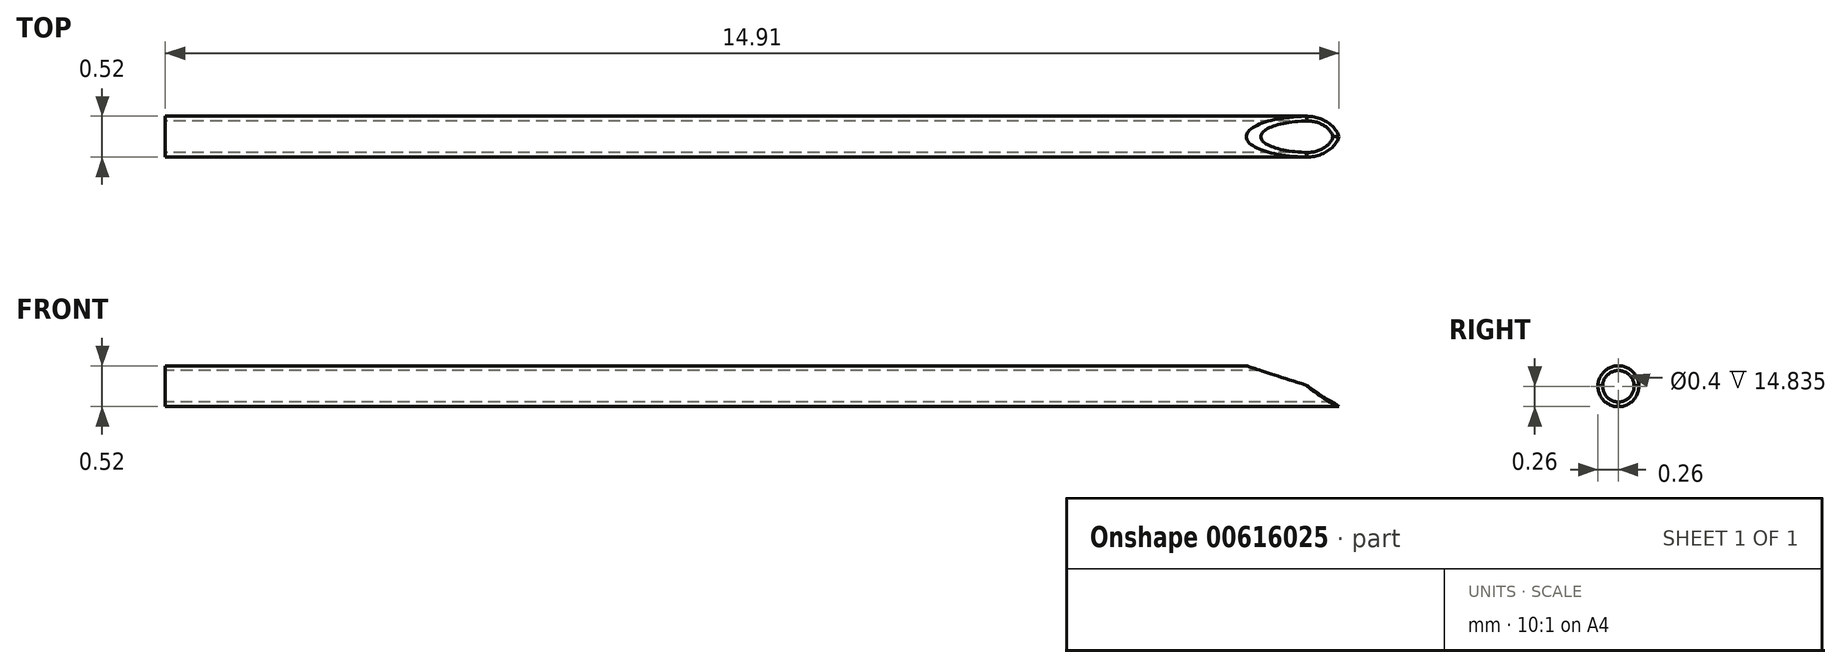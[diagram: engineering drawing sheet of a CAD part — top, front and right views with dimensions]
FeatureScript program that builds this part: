
annotation { "Feature Type Name" : "Feature", "Feature Type Description" : "" }
export const myFeature = defineFeature(function(context is Context, id is Id, definition is map)
    precondition{}
    {
        {
            var Q0;
            Q0=qCreatedBy(makeId("Front.planeOp"),FACE);
            var sketch = newSketch(context, id + "F0", { "sketchPlane" : qUnion([Q0])});
            skLineSegment(sketch, "E0", {"start": v(-2.36, 0) * mm, "end": v(2.25, 0) * mm, "construction": true});
            skLineSegment(sketch, "E1", {"start": v(-1.77, 0.26) * mm, "end": v(14.23, 0.26) * mm});
            skLineSegment(sketch, "E2", {"start": v(14.23, 0.2) * mm, "end": v(-1.77, 0.2) * mm});
            skLineSegment(sketch, "E3", {"start": v(-1.77, 0.2) * mm, "end": v(-1.77, 0.26) * mm});
            skLineSegment(sketch, "E4", {"start": v(14.23, 0.26) * mm, "end": v(14.23, 0.2) * mm});
            skSolve(sketch);
        }
        {
            var Q0;
            Q0 = qSketchRegion(id + "F0", true);
            var Q1;
            Q1=sQuery(id+"F0.wireOp",EDGE,"E0");
            revolve(context, id + "F1", {"entities" : qUnion([Q0]), "axis" : qUnion([Q1]), "revolveType" : RevolveType.FULL});
        }
        {
            var Q0;
            Q0=qCreatedBy(makeId("Front.planeOp"),FACE);
            var sketch = newSketch(context, id + "F2", { "sketchPlane" : qUnion([Q0])});
            skLineSegment(sketch, "E5", {"start": v(6, 2.2) * mm, "end": v(15.66, 2.2) * mm});
            skLineSegment(sketch, "E6", {"start": v(6, 2.2) * mm, "end": v(15.66, -0.94) * mm});
            skLineSegment(sketch, "E7", {"start": v(15.66, -0.94) * mm, "end": v(15.66, 2.2) * mm});
            skPoint(sketch, "E8.orphan", {"position": v(16.03, 2.2) * mm});
            skSolve(sketch);
        }
        {
            var Q0;
            Q0 = qSketchRegion(id + "F2", true);
            extrude(context, id + "F3", {"entities" : qUnion([Q0]), "operationType" : NewBodyOperationType.REMOVE, "depth" : 25 * mm, "offsetDistance" : 25 * mm, "symmetric" : true});
        }
        {
            var Q0;
            Q0=qCreatedBy(makeId("Front.planeOp"),FACE);
            var sketch = newSketch(context, id + "F4", { "sketchPlane" : qUnion([Q0])});
            skLineSegment(sketch, "E9", {"start": v(9.44, 2.63) * mm, "end": v(14.6, -1.4) * mm});
            skLineSegment(sketch, "E10", {"start": v(14.6, -1.4) * mm, "end": v(14.6, 2.63) * mm});
            skLineSegment(sketch, "E11", {"start": v(14.6, 2.63) * mm, "end": v(9.44, 2.63) * mm});
            skSolve(sketch);
        }
        {
            var Q0;
            Q0 = qSketchRegion(id + "F4", true);
            extrude(context, id + "F5", {"entities" : qUnion([Q0]), "operationType" : NewBodyOperationType.REMOVE, "oppositeDirection" : true, "depth" : 2 * mm, "offsetDistance" : 25 * mm, "hasDraft" : true, "draftAngle" : 10 * degree, "symmetric" : true});
        }
    });
